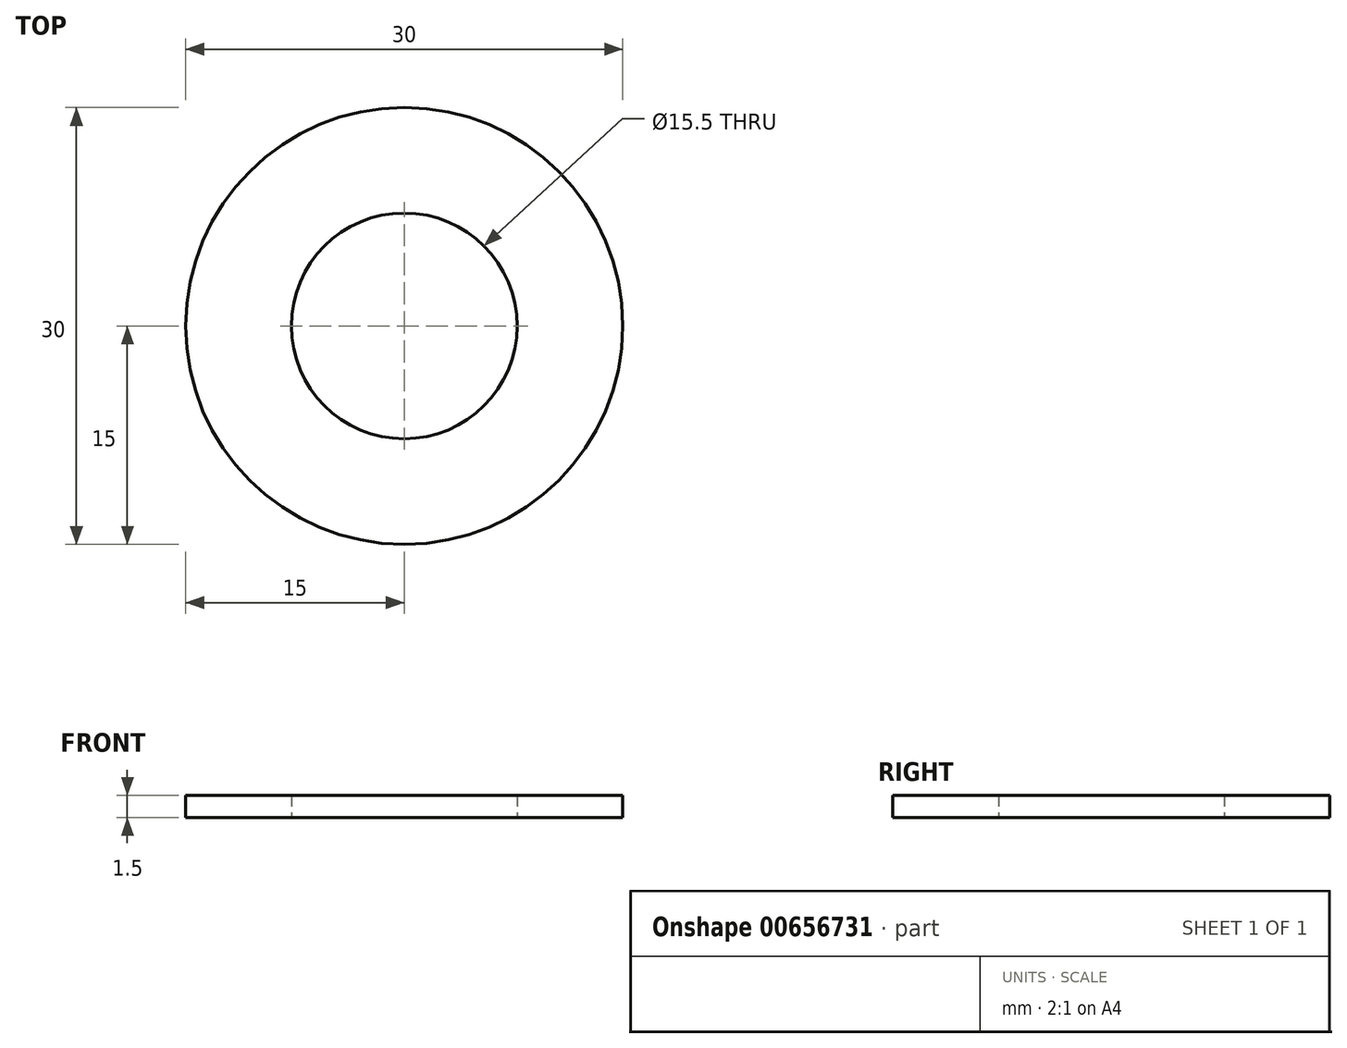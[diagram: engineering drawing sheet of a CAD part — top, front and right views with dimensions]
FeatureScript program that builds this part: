
annotation { "Feature Type Name" : "Feature", "Feature Type Description" : "" }
export const myFeature = defineFeature(function(context is Context, id is Id, definition is map)
    precondition{}
    {
        {
            var Q0;
            Q0=qCreatedBy(makeId("Top.planeOp"),FACE);
            var sketch = newSketch(context, id + "F0", { "sketchPlane" : qUnion([Q0])});
            skCircle(sketch, "E0", {"center": v(0, 0) * mm, "radius": 15 * mm});
            skCircle(sketch, "E1", {"center": v(0, 0) * mm, "radius": 7.75 * mm});
            skSolve(sketch);
        }
        {
            var Q0;
            Q0=makeQuery(id+"F0.imprint","IMPRINT",FACE,{"disambiguationData":[TD([[makeQuery(id+"F0.imprint","IMPRINT",EDGE,{"derivedFrom":sQuery(id+"F0.wireOp",EDGE,"E0")}),1.0]])]});
            extrude(context, id + "F1", {"entities" : qUnion([Q0]), "depth" : 1.5 * mm, "offsetDistance" : 25 * mm});
        }
    });
